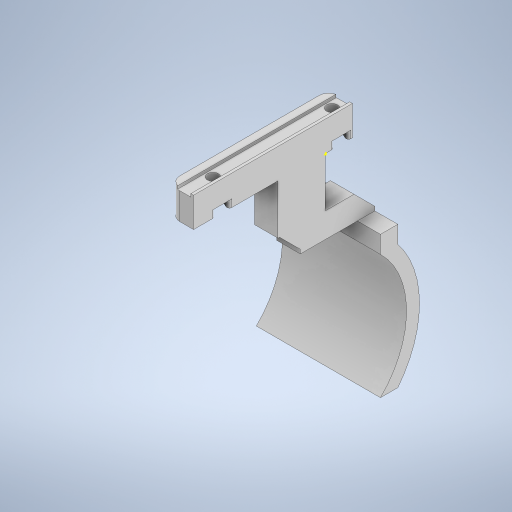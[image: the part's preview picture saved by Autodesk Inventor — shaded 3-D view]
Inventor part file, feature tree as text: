
AUTODESK INVENTOR PART (.ipt)
format: ipt  version: 2024 (Build 280153000, 153)  size: 373,248 bytes
history: native  units: in
note: dims shown in document units (in); Inventor stores cm internally (conversion verified against a paired STEP export)
features: sketch x10, extrude x7, projected_geometry x4, fillet x2, chamfer x2, sweep x1
ambient origin geometry x8: Origin, YZ Plane, XZ Plane, XY Plane, X Axis, Y Axis, Z Axis, Center Point
bodies: Solid1 (feature_tree)
feature tree (26):
  extrude  "Extrusion1"  Depth=2.5197in
  extrude  "Extrusion2"  Depth=1.8898in
  extrude  "Extrusion3"  Depth=0.4724in TaperAngle=0.0deg
  fillet  "Fillet1"  Radius=0.0433in
  fillet  "Fillet2"  Radius=0.2126in
  extrude  "Extrusion19"  Depth=0.4724in TaperAngle=0.0deg
  extrude  "Extrusion21"  Depth=0.1181in TaperAngle=0.0deg
  sketch  "Sketch41"  dims[d17=0.1772in d18=0.0394in]
  extrude  "Extrusion22"  Depth=0.0394in
  sweep  "Sweep3"
  extrude  "Extrusion25"  Depth=0.748in
  chamfer  "Chamfer4"  Distance=0.7874in
  chamfer  "Chamfer5"  Distance=0.3937in
  sketch  "Sketch1"  dims[d1=0.374in d2=2.5197in]
  sketch  "Sketch2"  dims[d3=0.1772in d4=1.8898in]
  sketch  "Sketch3"  dims[d6=0.1457in d7=0.4724in d8=0.0in d9=0.0433in d10=0.2126in]
  projected_geometry  "Projected Loop2"
  projected_geometry  "Projected Loop3"
  projected_geometry  "Projected Loop4"
  projected_geometry  "Projected Loop5"
  sketch  "Sketch28"  dims[d11=0.0472in d12=0.4724in d13=0.0in]
  sketch  "Sketch40"  dims[d14=0.2953in d15=0.1181in d16=0.0in]
  sketch  "Sketch42"  dims[d19=0.1575in d76=0.4724in]
  sketch  "Sketch43"  dims[d107=0.102in d108=0.748in d109=0.7874in d110=0.0in]
  sketch  "Sketch44"  dims[d130=0.7874in]
  sketch  "Sketch54"  dims[d131=1.1811in d132=0.3937in d133=0.0in d134=1.2283in d135=180.0deg d136=0.2756in d137=1.9685in d138=0.2756in d139=0.2756in d140=0.0in d141=1.9685in d142=1.378in d143=0.0in d144=0.0in d154=4.1063in d155=0.0in d156=0.3287in d157=0.0787in d158=45.0deg d159=0.3287in d160=0.0787in d161=45.0deg d42=0.0197in d43=0.0344in d44=0.0197in d45=0.0344in d46=0.0in d47=0.0in d48=0.0in d49=0.0in d50=0.0in d51=0.0in d52=0.0in d53=0.0in d55=0.0197in d56=0.0344in d57=0.0197in d58=0.0344in d60=0.0197in d61=0.0344in d62=0.0197in d63=0.0344in d72=0.0197in d73=0.0344in d74=0.0197in d75=0.0344in]
